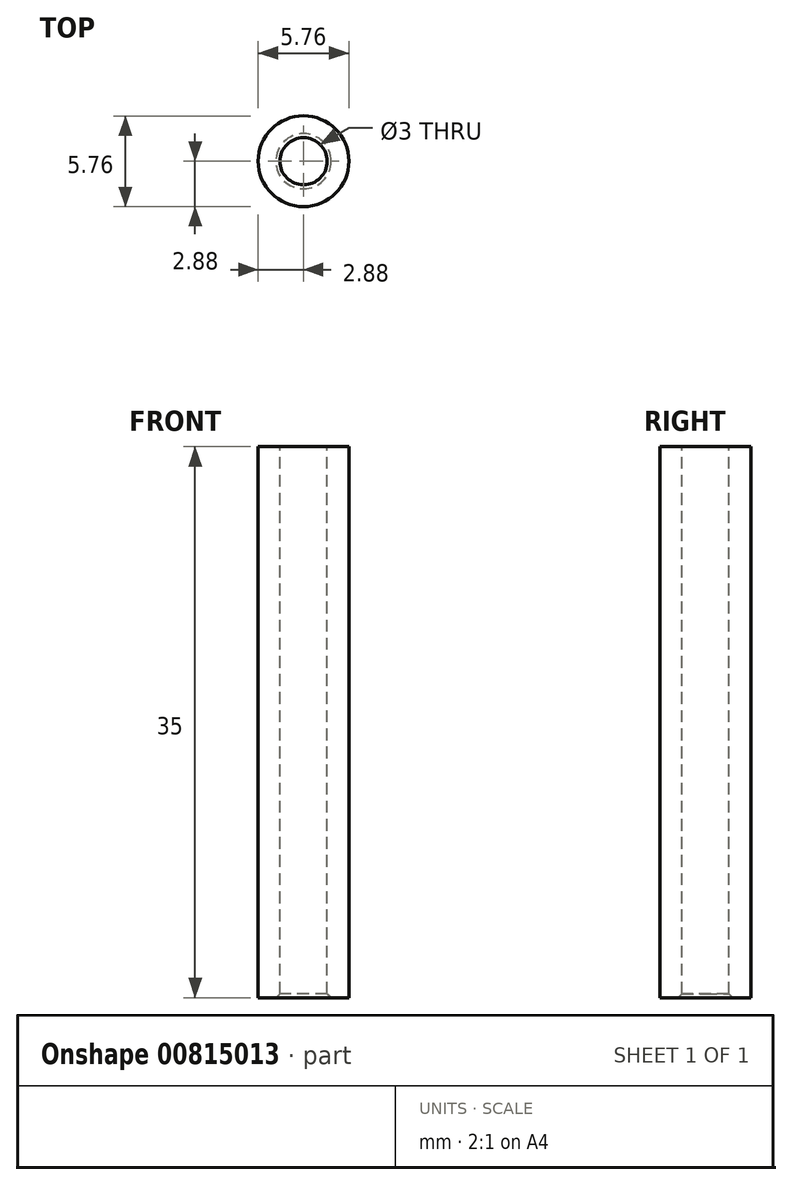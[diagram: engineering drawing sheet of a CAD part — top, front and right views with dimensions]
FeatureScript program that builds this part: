
annotation { "Feature Type Name" : "Feature", "Feature Type Description" : "" }
export const myFeature = defineFeature(function(context is Context, id is Id, definition is map)
    precondition{}
    {
        {
            var Q0;
            Q0=qCreatedBy(makeId("Top.planeOp"),FACE);
            var sketch = newSketch(context, id + "F0", { "sketchPlane" : qUnion([Q0])});
            skCircle(sketch, "E0.cCircle", {"center": v(0, 0) * mm, "radius": 2.88 * mm});
            skSolve(sketch);
        }
        {
            var Q0;
            Q0=qSketchRegion(id+"F0",true);
            extrude(context, id + "F1", {"entities" : qUnion([Q0]), "endBound" : BoundingType.SYMMETRIC, "depth" : 35 * mm});
        }
        {
            var Q0;
            Q0=makeQuery(id+"F1.opExtrude","CAP_FACE",FACE,{"disambiguationData":[OSD([sQuery(id+"F0.wireOp",EDGE,"E0.cCircle")])],"isStart":false});
            var sketch = newSketch(context, id + "F2", { "sketchPlane" : qUnion([Q0])});
            skCircle(sketch, "E1", {"center": v(0, 0) * mm, "radius": 1.5 * mm});
            skSolve(sketch);
        }
        {
            var Q0;
            Q0=qSketchRegion(id+"F2",true);
            extrude(context, id + "F3", {"entities" : qUnion([Q0]), "operationType" : NewBodyOperationType.REMOVE, "endBound" : BoundingType.THROUGH_ALL, "oppositeDirection" : true, "depth" : 9.52 * mm, "offsetDistance" : 25 * mm});
        }
        {
            var Q0;
            Q0=makeQuery(id+"F3.boolean.opBoolean","COPY",EDGE,{"derivedFrom":makeQuery(id+"F3.opExtrude","CAP_EDGE",EDGE,{"disambiguationData":[OSD([sQuery(id+"F2.wireOp",EDGE,"E1")])],"isStart":true})});
            var Q1;
            Q1=makeQuery(id+"F3.boolean.opBoolean","INTERSECT",EDGE,{"derivedFrom":[makeQuery(id+"F1.opExtrude","CAP_FACE",FACE,{"disambiguationData":[OSD([sQuery(id+"F0.wireOp",EDGE,"E0.cCircle")])],"isStart":true}),makeQuery(id+"F3.opExtrude","SWEPT_FACE",FACE,{"disambiguationData":[OSD([sQuery(id+"F2.wireOp",EDGE,"E1")])]})]});
            chamfer(context, id + "F4", {"entities" : qUnion([Q0, Q1]), "width" : 0.25 * mm, "tangentPropagation" : true});
        }
    });
